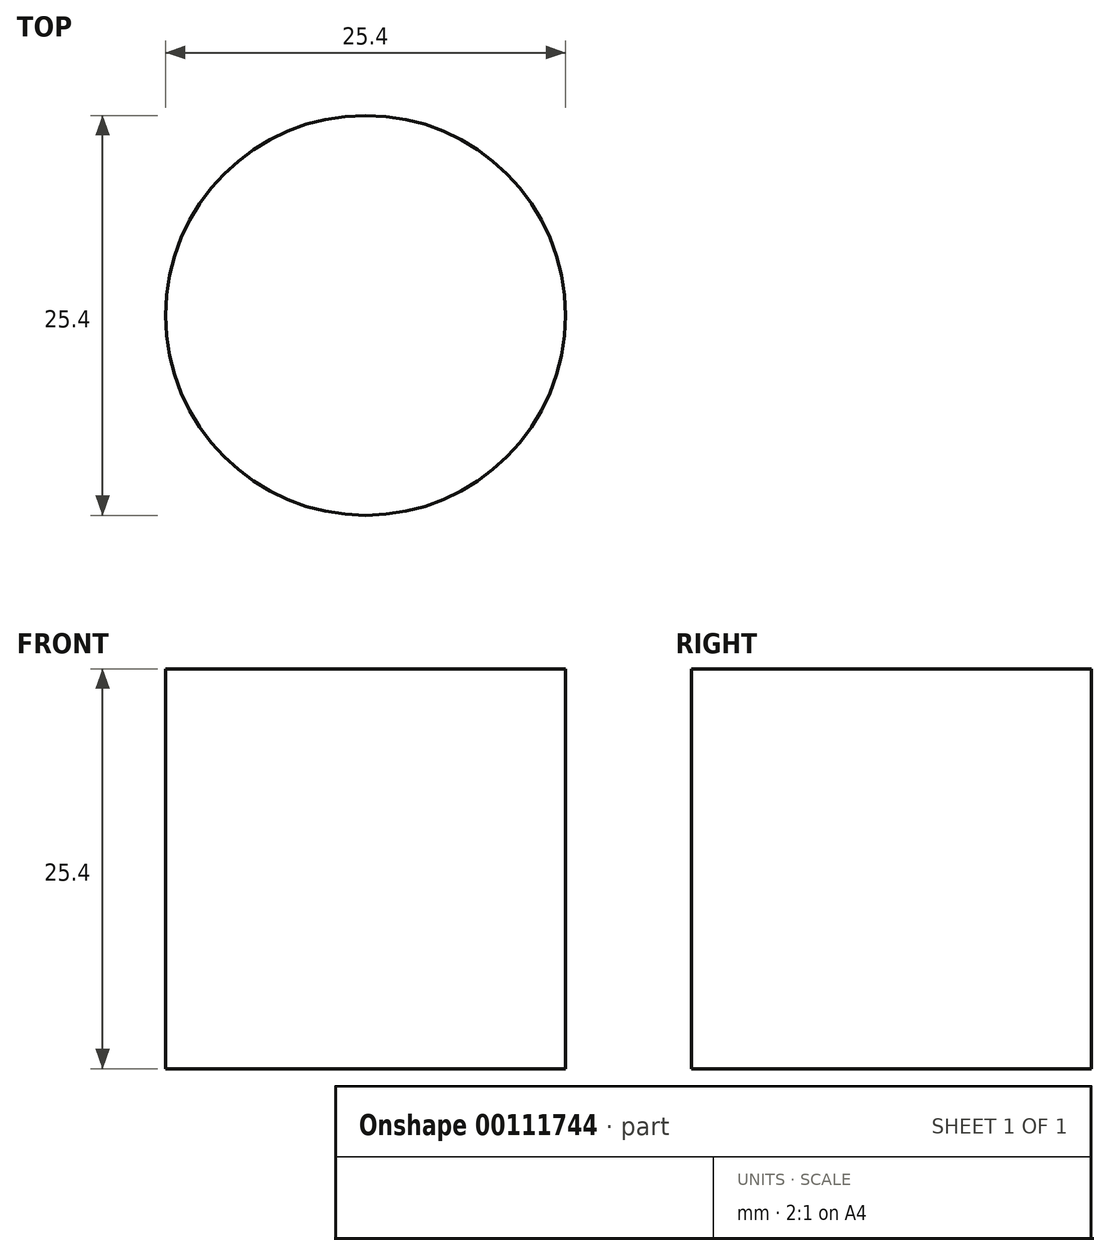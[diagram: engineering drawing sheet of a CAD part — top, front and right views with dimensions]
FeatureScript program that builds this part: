
annotation { "Feature Type Name" : "Feature", "Feature Type Description" : "" }
export const myFeature = defineFeature(function(context is Context, id is Id, definition is map)
    precondition{}
    {
        {
            var Q0;
            Q0=qCreatedBy(makeId("Top.planeOp"),FACE);
            var sketch = newSketch(context, id + "F0", { "sketchPlane" : qUnion([Q0])});
            skCircle(sketch, "E0", {"center": v(0, 0) * mm, "radius": 12.7 * mm});
            skSolve(sketch);
        }
        {
            var Q0;
            Q0=makeQuery(id+"F0.imprint","IMPRINT",FACE,{"disambiguationData":[TD([[makeQuery(id+"F0.imprint","IMPRINT",EDGE,{"derivedFrom":sQuery(id+"F0.wireOp",EDGE,"E0")}),1.0]])]});
            extrude(context, id + "F1", {"entities" : qUnion([Q0]), "depth" : 25.4 * mm});
        }
    });
